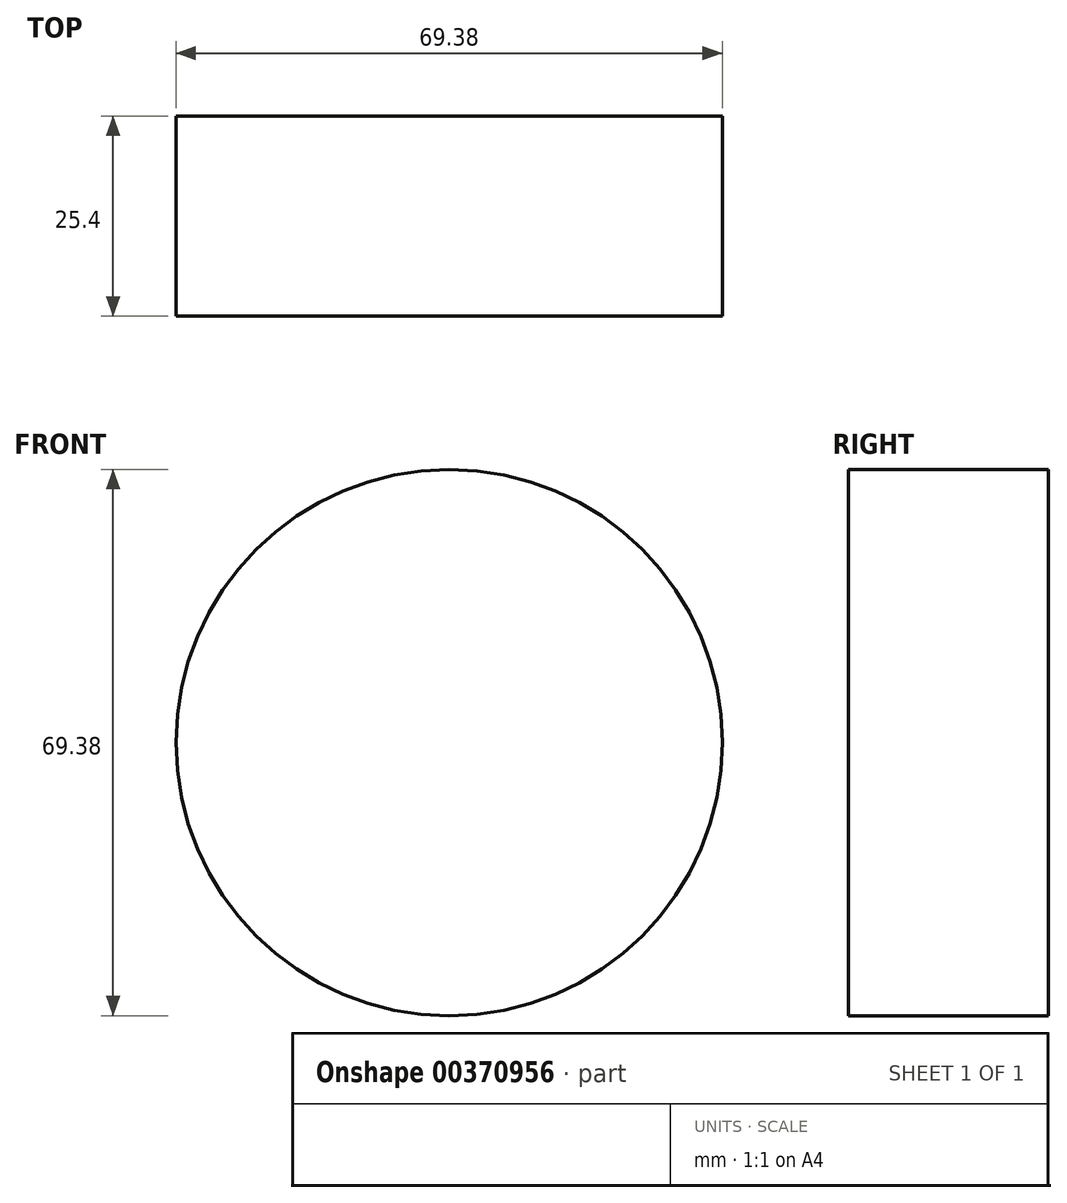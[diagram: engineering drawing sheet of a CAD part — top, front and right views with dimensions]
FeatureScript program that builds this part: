
annotation { "Feature Type Name" : "Feature", "Feature Type Description" : "" }
export const myFeature = defineFeature(function(context is Context, id is Id, definition is map)
    precondition{}
    {
        {
            var Q0;
            Q0=qCreatedBy(makeId("Front.planeOp"),FACE);
            var sketch = newSketch(context, id + "F0", { "sketchPlane" : qUnion([Q0])});
            skCircle(sketch, "E0", {"center": v(0, 0) * mm, "radius": 34.7 * mm});
            skSolve(sketch);
        }
        {
            var Q0;
            Q0 = qSketchRegion(id + "F0", true);
            var Q1;
            Q1=makeQuery(id+"F0.imprint","IMPRINT",FACE,{"disambiguationData":[TD([[makeQuery(id+"F0.imprint","IMPRINT",EDGE,{"derivedFrom":sQuery(id+"F0.wireOp",EDGE,"E0")}),1.0]])]});
            extrude(context, id + "F1", {"entities" : qUnion([Q0, Q1]), "depth" : 25.4 * mm});
        }
    });
